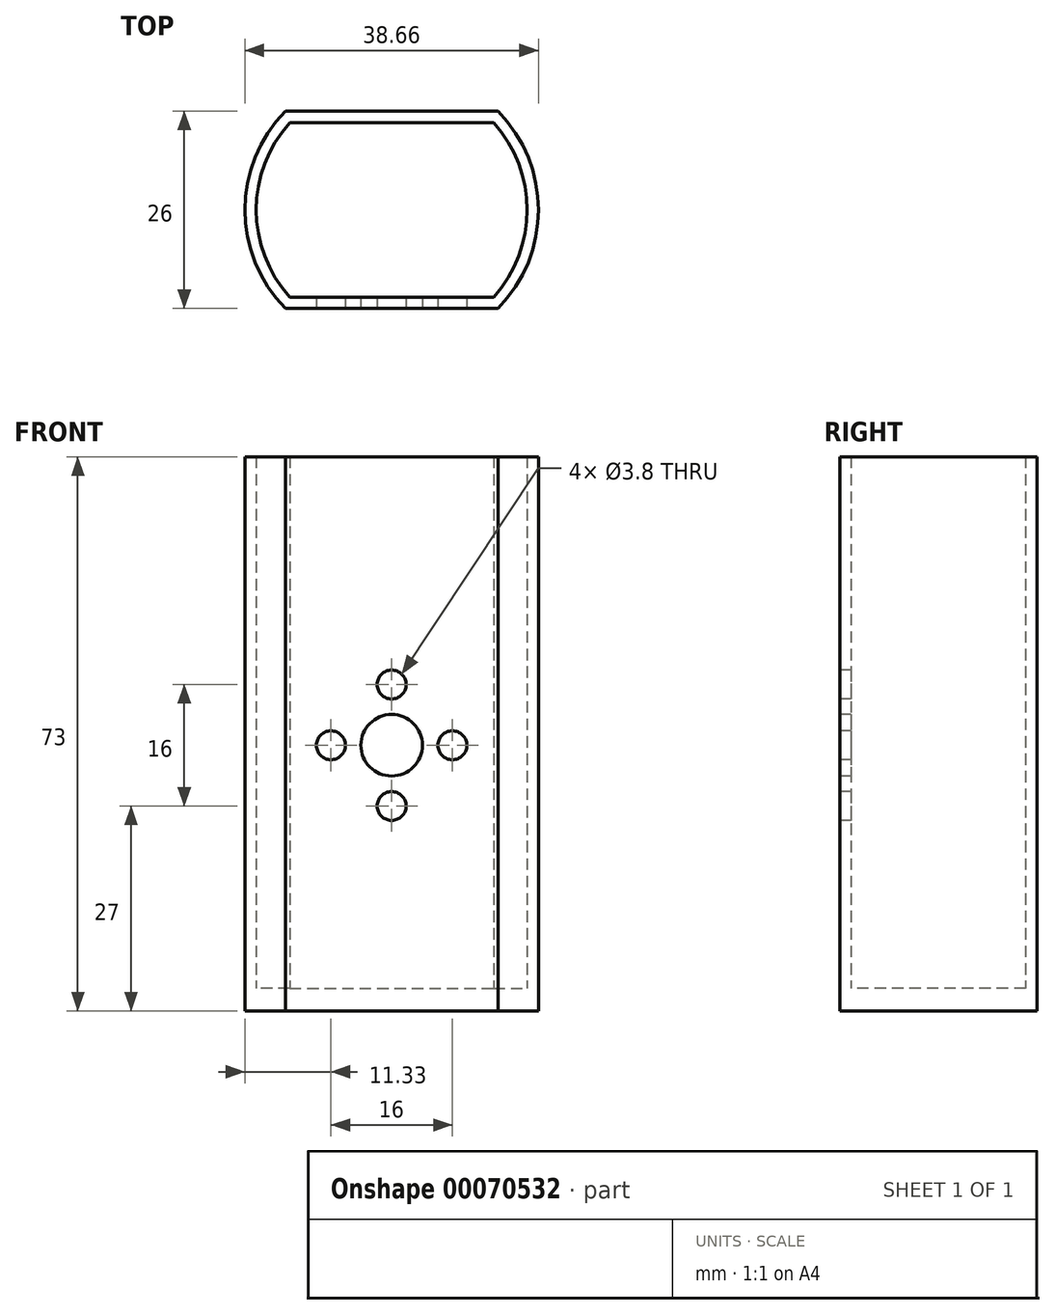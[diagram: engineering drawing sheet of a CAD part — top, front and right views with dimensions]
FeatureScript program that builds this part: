
annotation { "Feature Type Name" : "Feature", "Feature Type Description" : "" }
export const myFeature = defineFeature(function(context is Context, id is Id, definition is map)
    precondition{}
    {
        {
            var Q0;
            Q0=qCreatedBy(makeId("Top.planeOp"),FACE);
            var sketch = newSketch(context, id + "F0", { "sketchPlane" : qUnion([Q0])});
            skPoint(sketch, "E0.rect.middle", {"position": v(0, 0) * mm});
            skArc(sketch, "E1", {"start": v(-14, 13) * mm, "mid": v(-19.33, 0) * mm, "end": v(-14, -13) * mm});
            skArc(sketch, "E2.MirrorCS", {"start": v(14, 13) * mm, "mid": v(19.33, 0) * mm, "end": v(14, -13) * mm});
            skLineSegment(sketch, "E3", {"start": v(-14, -13) * mm, "end": v(14, -13) * mm});
            skLineSegment(sketch, "E4", {"start": v(14, 13) * mm, "end": v(-14, 13) * mm});
            skSolve(sketch);
        }
        {
            var Q0;
            Q0=makeQuery(id+"F0.imprint","IMPRINT",FACE,{"disambiguationData":[TD([[makeQuery(id+"F0.imprint","IMPRINT",EDGE,{"derivedFrom":sQuery(id+"F0.wireOp",EDGE,"E0.rect.bottom")}),1.0]])]});
            var Q1;
            Q1=makeQuery(id+"F0.imprint","IMPRINT",FACE,{"disambiguationData":[TD([[makeQuery(id+"F0.imprint","IMPRINT",EDGE,{"derivedFrom":sQuery(id+"F0.wireOp",EDGE,"E1")}),1.0]])]});
            extrude(context, id + "F1", {"entities" : qUnion([Q0, Q1]), "depth" : 3 * mm});
        }
        {
            var Q0;
            Q0=makeQuery(id+"F1.opExtrude","CAP_FACE",FACE,{"disambiguationData":[OSD([sQuery(id+"F0.wireOp",EDGE,"E1"),sQuery(id+"F0.wireOp",EDGE,"E2.MirrorCS"),sQuery(id+"F0.wireOp",EDGE,"E3"),sQuery(id+"F0.wireOp",EDGE,"E4")])],"isStart":false});
            var sketch = newSketch(context, id + "F2", { "sketchPlane" : qUnion([Q0])});
            skPoint(sketch, "E5.rect.middle", {"position": v(0, 0) * mm});
            skLineSegment(sketch, "E6", {"start": v(-19.33, 0) * mm, "end": v(-17.83, 0) * mm, "construction": true});
            skLineSegment(sketch, "E7.rect.bottom", {"start": v(-13.42, -11.5) * mm, "end": v(13.42, -11.5) * mm});
            skLineSegment(sketch, "E7.rect.top", {"start": v(-13.42, 11.5) * mm, "end": v(13.42, 11.5) * mm});
            skArc(sketch, "E8", {"start": v(-13.42, 11.5) * mm, "mid": v(-17.83, 0) * mm, "end": v(-13.42, -11.5) * mm});
            skArc(sketch, "E9.MirrorCS", {"start": v(13.42, 11.5) * mm, "mid": v(17.83, 0) * mm, "end": v(13.42, -11.5) * mm});
            skSolve(sketch);
        }
        {
            var Q0;
            Q0=makeQuery(id+"F2.imprint","IMPRINT",FACE,{"disambiguationData":[TD([[makeQuery(id+"F2.imprint","IMPRINT",EDGE,{"derivedFrom":sQuery(id+"F2.wireOp",EDGE,"E5.rect.bottom")}),-1.0]])]});
            var Q1;
            Q1=makeQuery(id+"F2.imprint","IMPRINT",FACE,{"disambiguationData":[TD([[makeQuery(id+"F2.imprint","IMPRINT",EDGE,{"derivedFrom":sQuery(id+"F2.wireOp",EDGE,"E7.rect.bottom")}),-1.0]])]});
            extrude(context, id + "F3", {"entities" : qUnion([Q0, Q1]), "operationType" : NewBodyOperationType.ADD, "depth" : 70 * mm});
        }
        {
            var Q0;
            {var subQ0=sQuery(id+"F0.wireOp",EDGE,"E3");Q0=makeQuery(id+"F3.boolean.opBoolean","MERGE",FACE,{"derivedFrom":[makeQuery(id+"F1.opExtrude","SWEPT_FACE",FACE,{"disambiguationData":[OSD([subQ0])]}),makeQuery(id+"F3.opExtrude","SWEPT_FACE",FACE,{"disambiguationData":[OSD([subQ0])]})]});}
            var sketch = newSketch(context, id + "F4", { "sketchPlane" : qUnion([Q0])});
            skLineSegment(sketch, "E10", {"start": v(0, 0) * mm, "end": v(0, 35) * mm, "construction": true});
            skCircle(sketch, "E11", {"center": v(0, 35) * mm, "radius": 4.05 * mm});
            skLineSegment(sketch, "E12", {"start": v(0, 35) * mm, "end": v(0, 43) * mm, "construction": true});
            skCircle(sketch, "E13", {"center": v(0, 43) * mm, "radius": 1.9 * mm});
            skCircle(sketch, "E14.1.0", {"center": v(-8, 35) * mm, "radius": 1.9 * mm});
            skCircle(sketch, "E14.2.0", {"center": v(0, 27) * mm, "radius": 1.9 * mm});
            skCircle(sketch, "E14.3.0", {"center": v(8, 35) * mm, "radius": 1.9 * mm});
            skSolve(sketch);
        }
        {
            var Q0;
            Q0=makeQuery(id+"F4.imprint","IMPRINT",FACE,{"disambiguationData":[TD([[makeQuery(id+"F4.imprint","IMPRINT",EDGE,{"derivedFrom":sQuery(id+"F4.wireOp",EDGE,"E14.1.0")}),1.0]])]});
            var Q1;
            Q1=makeQuery(id+"F4.imprint","IMPRINT",FACE,{"disambiguationData":[TD([[makeQuery(id+"F4.imprint","IMPRINT",EDGE,{"derivedFrom":sQuery(id+"F4.wireOp",EDGE,"E11")}),1.0]])]});
            var Q2;
            Q2=makeQuery(id+"F4.imprint","IMPRINT",FACE,{"disambiguationData":[TD([[makeQuery(id+"F4.imprint","IMPRINT",EDGE,{"derivedFrom":sQuery(id+"F4.wireOp",EDGE,"E14.3.0")}),1.0]])]});
            var Q3;
            Q3=makeQuery(id+"F4.imprint","IMPRINT",FACE,{"disambiguationData":[TD([[makeQuery(id+"F4.imprint","IMPRINT",EDGE,{"derivedFrom":sQuery(id+"F4.wireOp",EDGE,"E13")}),1.0]])]});
            var Q4;
            Q4=makeQuery(id+"F4.imprint","IMPRINT",FACE,{"disambiguationData":[TD([[makeQuery(id+"F4.imprint","IMPRINT",EDGE,{"derivedFrom":sQuery(id+"F4.wireOp",EDGE,"E14.2.0")}),1.0]])]});
            extrude(context, id + "F5", {"entities" : qUnion([Q0, Q1, Q2, Q3, Q4]), "operationType" : NewBodyOperationType.REMOVE, "oppositeDirection" : true, "depth" : 4 * mm});
        }
    });
